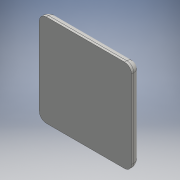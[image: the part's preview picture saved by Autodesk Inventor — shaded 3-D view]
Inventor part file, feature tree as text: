
AUTODESK INVENTOR PART (.ipt)
format: ipt  version: 2016 (Build 200138000, 138)  size: 106,496 bytes
history: native  units: mm
features: extrude x1, fillet x1, sketch x1
ambient origin geometry x8: Origin, YZ Plane, XZ Plane, XY Plane, X Axis, Y Axis, Z Axis, Center Point
bodies: Solid1 (feature_tree)
feature tree (3):
  extrude  "Extrusion1"  Depth=40.0mm
  fillet  "Fillet1"  Radius=4.0mm
  sketch  "Sketch2"  dims[d6=40.0mm d7=40.0mm d8=4.0mm d9=0.0mm d10=3.0mm]
